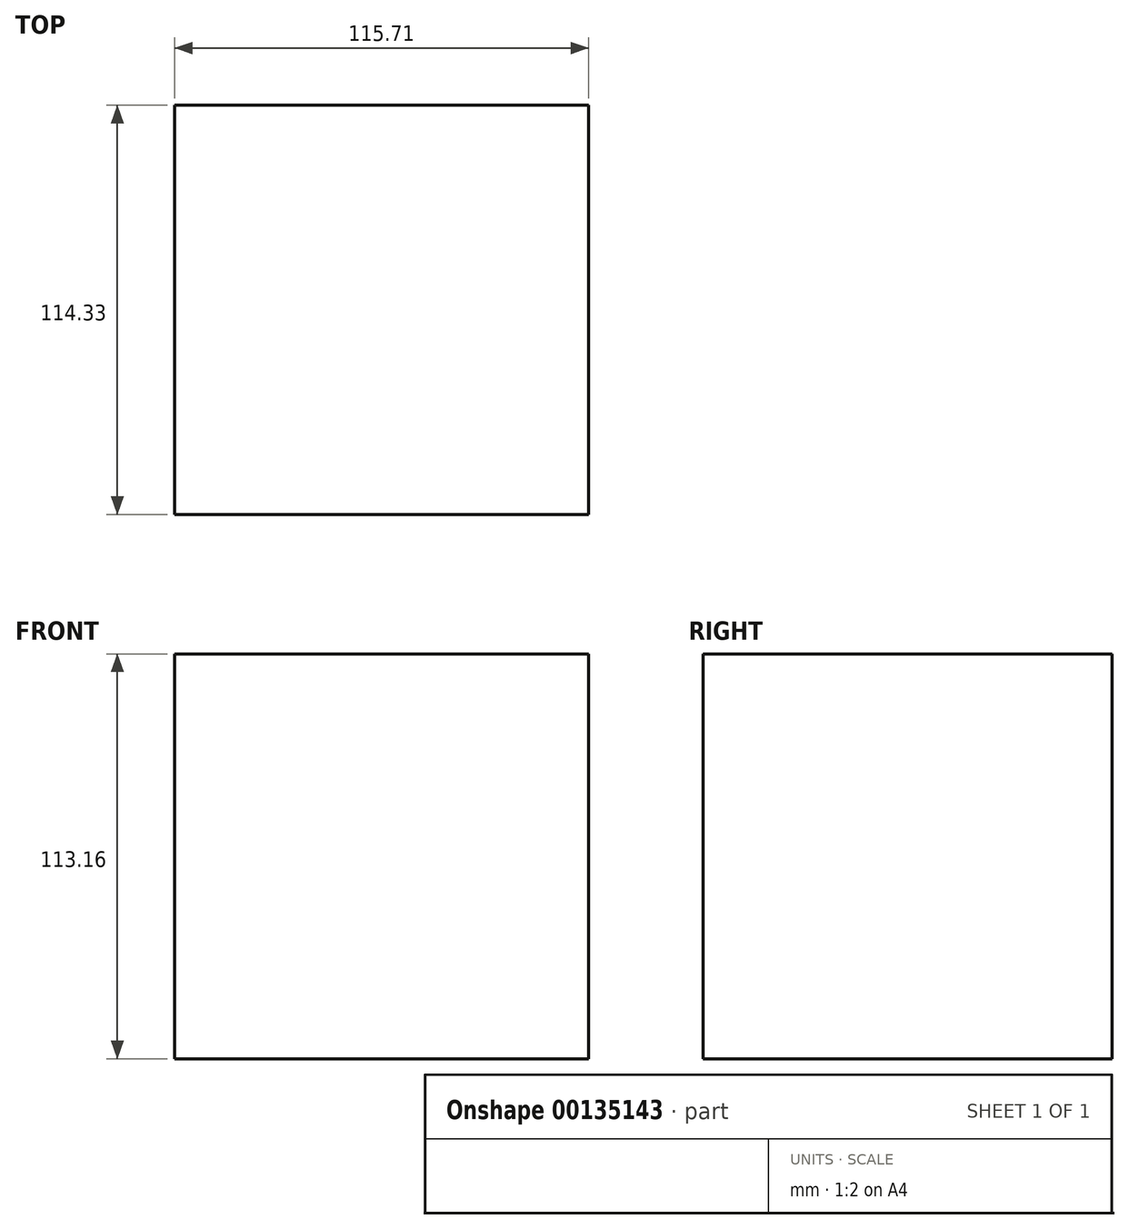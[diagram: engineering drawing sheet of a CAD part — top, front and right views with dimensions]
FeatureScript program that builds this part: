
annotation { "Feature Type Name" : "Feature", "Feature Type Description" : "" }
export const myFeature = defineFeature(function(context is Context, id is Id, definition is map)
    precondition{}
    {
        {
            var Q0;
            Q0=qCreatedBy(makeId("Top.planeOp"),FACE);
            var sketch = newSketch(context, id + "F0", { "sketchPlane" : qUnion([Q0])});
            skLineSegment(sketch, "E0.bottom", {"start": v(123.64, 59.2) * mm, "end": v(7.93, 59.2) * mm});
            skLineSegment(sketch, "E0.top", {"start": v(123.64, -55.13) * mm, "end": v(7.93, -55.13) * mm});
            skLineSegment(sketch, "E0.left", {"start": v(123.64, 59.2) * mm, "end": v(123.64, -55.13) * mm});
            skLineSegment(sketch, "E0.right", {"start": v(7.93, 59.2) * mm, "end": v(7.93, -55.13) * mm});
            skSolve(sketch);
        }
        {
            var Q0;
            Q0=makeQuery(id+"F0.imprint","IMPRINT",FACE,{"disambiguationData":[TD([[makeQuery(id+"F0.imprint","IMPRINT",EDGE,{"derivedFrom":sQuery(id+"F0.wireOp",EDGE,"E0.bottom")}),1.0]])]});
            extrude(context, id + "F1", {"entities" : qUnion([Q0]), "depth" : 113.16 * mm});
        }
    });
